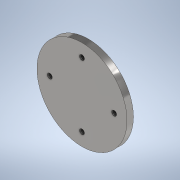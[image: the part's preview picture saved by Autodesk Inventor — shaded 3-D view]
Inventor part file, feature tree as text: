
AUTODESK INVENTOR PART (.ipt)
format: ipt  version: 2020 (Build 240168000, 168)  size: 118,784 bytes
history: native  units: mm
features: sketch x3, extrude x2, other x1, hole x1
ambient origin geometry x8: Origin, YZ Plane, XZ Plane, XY Plane, X Axis, Y Axis, Z Axis, Center Point
bodies: Body1 (feature_tree)
feature tree (7):
  other  "솔리드1"
  extrude  "돌출1"  Depth=10.0mm
  extrude  "돌출2"  Depth=3.0mm TaperAngle=0.0deg
  hole  "구멍1"  [1 undecoded]
  sketch  "스케치1"
  sketch  "스케치2"
  sketch  "스케치3"
note: 1 required parameter value undecoded (feature->parameter linkage not recoverable at this tier; creation-order binding heuristic only, values carry confidence <= 0.55)
